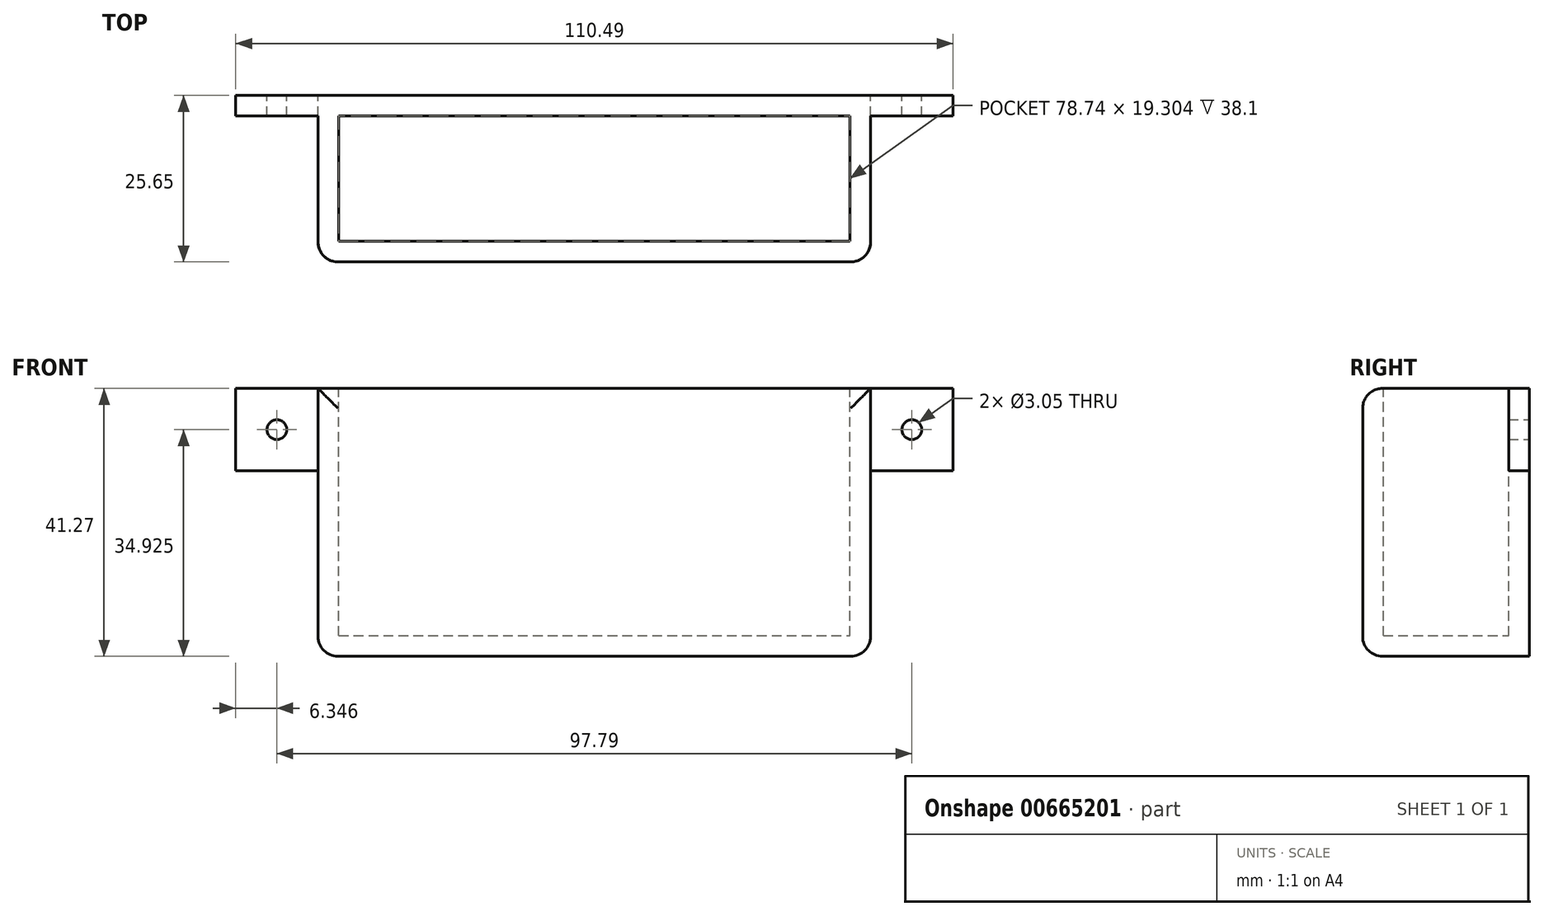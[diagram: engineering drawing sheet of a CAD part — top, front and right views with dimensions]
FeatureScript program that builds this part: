
annotation { "Feature Type Name" : "Feature", "Feature Type Description" : "" }
export const myFeature = defineFeature(function(context is Context, id is Id, definition is map)
    precondition{}
    {
        {
            var Q0;
            Q0=qCreatedBy(makeId("Front.planeOp"),FACE);
            var sketch = newSketch(context, id + "F0", { "sketchPlane" : qUnion([Q0])});
            skLineSegment(sketch, "E0.bottom", {"start": v(-1.81, 0) * mm, "end": v(83.28, 0) * mm});
            skLineSegment(sketch, "E0.top", {"start": v(-1.81, 41.27) * mm, "end": v(83.28, 41.27) * mm});
            skLineSegment(sketch, "E0.left", {"start": v(-1.81, 0) * mm, "end": v(-1.81, 41.27) * mm});
            skLineSegment(sketch, "E0.right", {"start": v(83.28, 0) * mm, "end": v(83.28, 41.27) * mm});
            skSolve(sketch);
        }
        {
            var Q0;
            Q0=makeQuery(id+"F0.imprint","IMPRINT",FACE,{"disambiguationData":[TD([[makeQuery(id+"F0.imprint","IMPRINT",EDGE,{"derivedFrom":sQuery(id+"F0.wireOp",EDGE,"E0.bottom")}),1.0]])]});
            extrude(context, id + "F1", {"entities" : qUnion([Q0]), "depth" : 25.65 * mm, "offsetDistance" : 25.4 * mm});
        }
        {
            var Q0;
            Q0=makeQuery(id+"F1.opExtrude","SWEPT_FACE",FACE,{"disambiguationData":[OSD([sQuery(id+"F0.wireOp",EDGE,"E0.top")])]});
            shell(context, id + "F2", {"entities" : qUnion([Q0]), "thickness" : 3.17 * mm});
        }
        {
            var Q0;
            Q0=makeQuery(id+"F1.opExtrude","CAP_FACE",FACE,{"disambiguationData":[OSD([sQuery(id+"F0.wireOp",EDGE,"E0.bottom"),sQuery(id+"F0.wireOp",EDGE,"E0.top"),sQuery(id+"F0.wireOp",EDGE,"E0.left"),sQuery(id+"F0.wireOp",EDGE,"E0.right")])],"isStart":true});
            var sketch = newSketch(context, id + "F3", { "sketchPlane" : qUnion([Q0])});
            skLineSegment(sketch, "E1.bottom", {"start": v(-83.28, 41.27) * mm, "end": v(-95.98, 41.27) * mm});
            skLineSegment(sketch, "E1.top", {"start": v(-83.28, 28.57) * mm, "end": v(-95.98, 28.57) * mm});
            skLineSegment(sketch, "E1.left", {"start": v(-83.28, 41.27) * mm, "end": v(-83.28, 28.57) * mm});
            skLineSegment(sketch, "E1.right", {"start": v(-95.98, 41.27) * mm, "end": v(-95.98, 28.57) * mm});
            skLineSegment(sketch, "E2.bottom", {"start": v(1.81, 41.27) * mm, "end": v(14.51, 41.27) * mm});
            skLineSegment(sketch, "E2.top", {"start": v(1.81, 28.57) * mm, "end": v(14.51, 28.57) * mm});
            skLineSegment(sketch, "E2.left", {"start": v(1.81, 41.27) * mm, "end": v(1.81, 28.57) * mm});
            skLineSegment(sketch, "E2.right", {"start": v(14.51, 41.27) * mm, "end": v(14.51, 28.57) * mm});
            skCircle(sketch, "E3", {"center": v(8.16, 34.92) * mm, "radius": 1.52 * mm});
            skCircle(sketch, "E4", {"center": v(-89.63, 34.92) * mm, "radius": 1.52 * mm});
            skSolve(sketch);
        }
        {
            var Q0;
            Q0=makeQuery(id+"F3.imprint","IMPRINT",FACE,{"disambiguationData":[TD([[makeQuery(id+"F3.imprint","IMPRINT",EDGE,{"derivedFrom":sQuery(id+"F3.wireOp",EDGE,"E2.bottom")}),-1.0]])]});
            var Q1;
            Q1=makeQuery(id+"F3.imprint","IMPRINT",FACE,{"disambiguationData":[TD([[makeQuery(id+"F3.imprint","IMPRINT",EDGE,{"derivedFrom":sQuery(id+"F3.wireOp",EDGE,"E1.bottom")}),1.0]])]});
            extrude(context, id + "F4", {"entities" : qUnion([Q0, Q1]), "operationType" : NewBodyOperationType.ADD, "oppositeDirection" : true, "depth" : 3.17 * mm, "offsetDistance" : 25.4 * mm});
        }
        {
            var Q0;
            Q0=makeQuery(id+"F1.opExtrude","CAP_FACE",FACE,{"disambiguationData":[OSD([sQuery(id+"F0.wireOp",EDGE,"E0.bottom"),sQuery(id+"F0.wireOp",EDGE,"E0.top"),sQuery(id+"F0.wireOp",EDGE,"E0.left"),sQuery(id+"F0.wireOp",EDGE,"E0.right")])],"isStart":false});
            var Q1;
            Q1=makeQuery(id+"F1.opExtrude","SWEPT_EDGE",EDGE,{"disambiguationData":[OSD([sQuery(id+"F0.wireOp",EDGE,"E0.bottom"),sQuery(id+"F0.wireOp",EDGE,"E0.right")])]});
            var Q2;
            Q2=makeQuery(id+"F1.opExtrude","SWEPT_EDGE",EDGE,{"disambiguationData":[OSD([sQuery(id+"F0.wireOp",EDGE,"E0.bottom"),sQuery(id+"F0.wireOp",EDGE,"E0.left")])]});
            fillet(context, id + "F5", {"entities" : qUnion([Q0, Q1, Q2]), "radius" : 3.05 * mm, "tangentPropagation" : true, "allowEdgeOverflow" : false});
        }
    });
